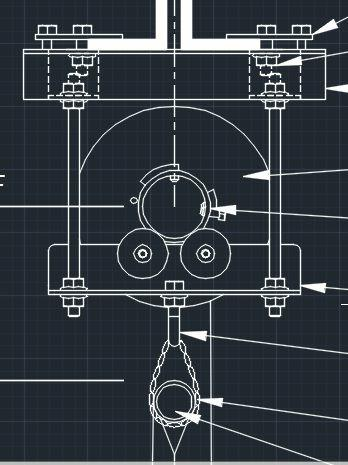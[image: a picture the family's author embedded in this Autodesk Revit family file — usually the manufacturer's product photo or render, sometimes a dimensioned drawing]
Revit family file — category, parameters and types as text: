
# Revit family: Gymnasium-Eqpt_Divider-Curtain_IPIbybison_RollUp
name_source: partatom
category: Specialty Equipment
revit_build: Autodesk Revit 2018 (Build: 20170927_1515(x64)
units: mm (PartAtom-declared; Revit-internal decimal feet)

## family parameters
Always vertical = Yes
Cut with Voids When Loaded = No
OmniClass Number = 23.40.50.34.17
OmniClass Title = Gymnasium Dividers
Part Type = Normal
Room Calculation Point = No
Round Connector Dimension = Use Diameter
Shared = No

## types (1)
- as Specified
    Available Options = as Specified
    Description = IPI by Bison Motorized Roll Up Divider Curtain - IP880 as Specified
    Expected Lifespan (Years) = 0
    Keynote = 11 66 53
    Maintenance Schedule (Months) = 0
    Manufacturer = IPI by Bison
    Manufacturer Fax = 800-638-0698
    Manufacturer Website = https://ipibybison.com
    Maximum Size = 36' Height x 120' Length
    Model = IP880
    Product Data = http://www.arcat.com
    Revision = R1_2018-06
    Sales Information = https://ipibybison.com
    URL = https://ipibybison.com
    Warranty Duration (Years) = 0

## geometry (parser evidence)
native form markers: Sweep x5
no freeform markers — native parametric forms only
